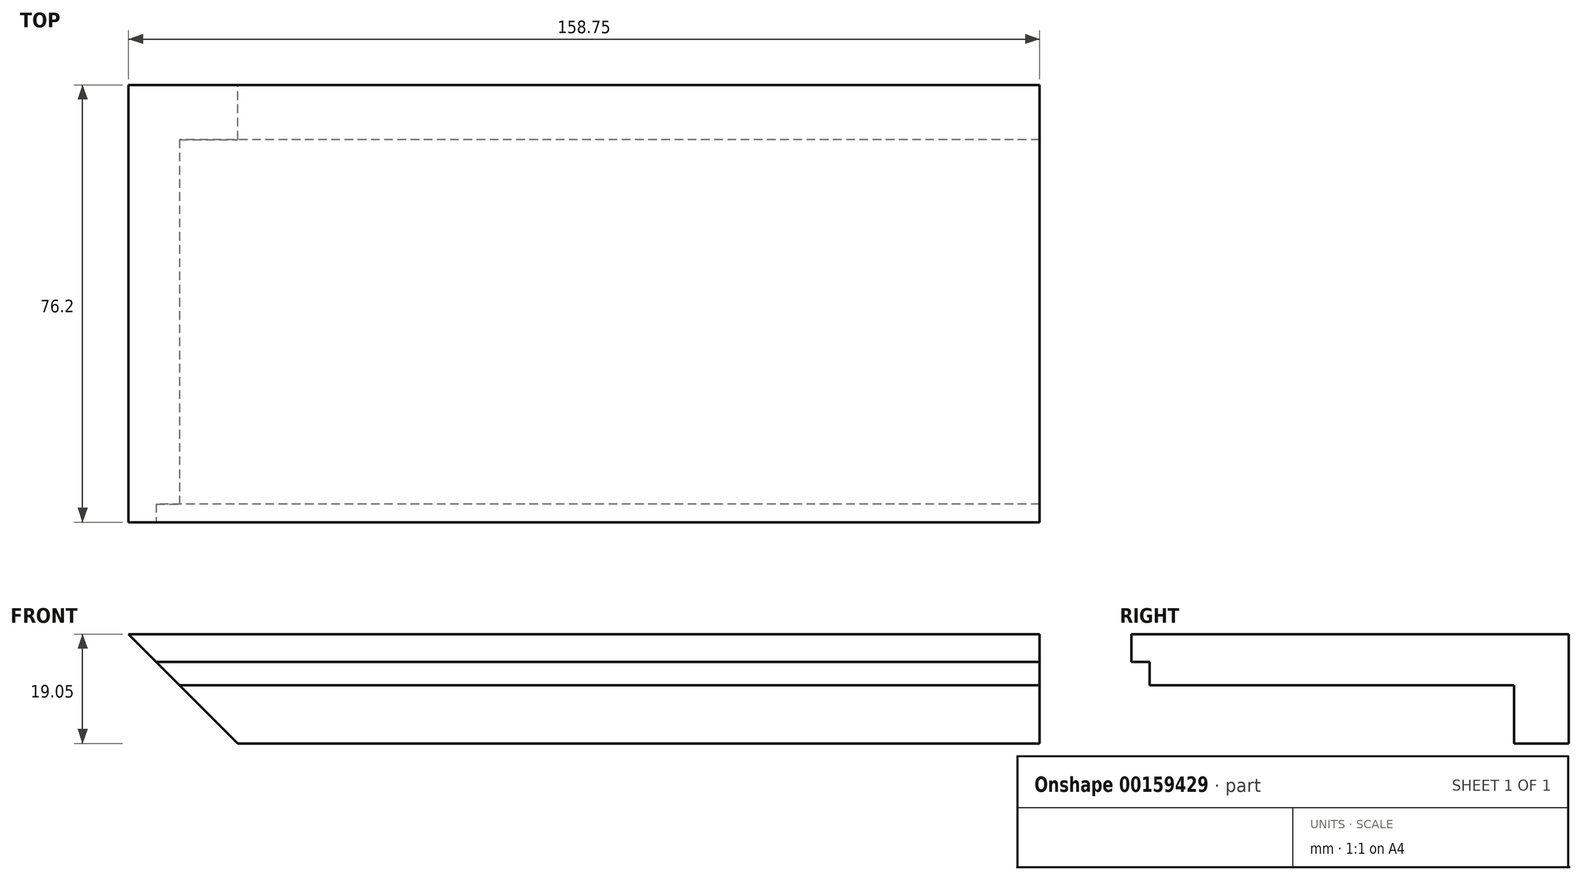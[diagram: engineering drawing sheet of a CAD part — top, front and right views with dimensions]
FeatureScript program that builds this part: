
annotation { "Feature Type Name" : "Feature", "Feature Type Description" : "" }
export const myFeature = defineFeature(function(context is Context, id is Id, definition is map)
    precondition{}
    {
        {
            var Q0;
            Q0=qCreatedBy(makeId("Front.planeOp"),FACE);
            var sketch = newSketch(context, id + "F0", { "sketchPlane" : qUnion([Q0])});
            skLineSegment(sketch, "E0", {"start": v(0, 180.55) * mm, "end": v(0, -185.02) * mm, "construction": true});
            skLineSegment(sketch, "E1", {"start": v(-187.82, 0) * mm, "end": v(184.46, 0) * mm, "construction": true});
            skLineSegment(sketch, "E2", {"start": v(0, 158.75) * mm, "end": v(-158.75, 158.75) * mm});
            skLineSegment(sketch, "E3", {"start": v(-158.75, 158.75) * mm, "end": v(-158.75, 0) * mm});
            skLineSegment(sketch, "E4", {"start": v(0, 139.7) * mm, "end": v(-139.7, 139.7) * mm});
            skLineSegment(sketch, "E5", {"start": v(-139.7, 139.7) * mm, "end": v(-139.7, 0) * mm});
            skLineSegment(sketch, "E6", {"start": v(-158.75, 0) * mm, "end": v(-139.7, 0) * mm});
            skLineSegment(sketch, "E7", {"start": v(0, 158.75) * mm, "end": v(0, 139.7) * mm});
            skSolve(sketch);
        }
        {
            var Q0;
            Q0=qSketchRegion(id+"F0",true);
            var Q1;
            Q1=qSketchRegion(id+"F2",true);
            extrude(context, id + "F1", {"entities" : qUnion([Q0, Q1]), "depth" : 76.2 * mm});
        }
        {
            var Q0;
            Q0=makeQuery(id+"F1.opExtrude","CAP_FACE",FACE,{"disambiguationData":[OSD([sQuery(id+"F0.wireOp",EDGE,"E2"),sQuery(id+"F0.wireOp",EDGE,"E3"),sQuery(id+"F0.wireOp",EDGE,"E4"),sQuery(id+"F0.wireOp",EDGE,"E5"),sQuery(id+"F0.wireOp",EDGE,"E6"),sQuery(id+"F0.wireOp",EDGE,"E7")])],"isStart":false});
            var sketch = newSketch(context, id + "F2", { "sketchPlane" : qUnion([Q0])});
            skLineSegment(sketch, "E8", {"start": v(0, -83.24) * mm, "end": v(0, 158.75) * mm, "construction": true});
            skLineSegment(sketch, "E9", {"start": v(-158.75, 0) * mm, "end": v(101.88, 0) * mm, "construction": true});
            skLineSegment(sketch, "E10.bottom", {"start": v(0, 0) * mm, "end": v(-153.92, 0) * mm});
            skLineSegment(sketch, "E10.top", {"start": v(0, 153.92) * mm, "end": v(-153.92, 153.92) * mm});
            skLineSegment(sketch, "E10.left", {"start": v(0, 0) * mm, "end": v(0, 153.92) * mm});
            skLineSegment(sketch, "E10.right", {"start": v(-153.92, 0) * mm, "end": v(-153.92, 153.92) * mm});
            skSolve(sketch);
        }
        {
            var Q0;
            Q0=qSketchRegion(id+"F2",true);
            extrude(context, id + "F3", {"entities" : qUnion([Q0]), "operationType" : NewBodyOperationType.REMOVE, "oppositeDirection" : true, "depth" : 3.17 * mm});
        }
        {
            var Q0;
            Q0=makeQuery(id+"F3.boolean.opBoolean","COPY",FACE,{"derivedFrom":makeQuery(id+"F3.opExtrude","CAP_FACE",FACE,{"disambiguationData":[OSD([sQuery(id+"F2.wireOp",EDGE,"E10.bottom"),sQuery(id+"F2.wireOp",EDGE,"E10.top"),sQuery(id+"F2.wireOp",EDGE,"E10.left"),sQuery(id+"F2.wireOp",EDGE,"E10.right")])],"isStart":false})});
            var sketch = newSketch(context, id + "F4", { "sketchPlane" : qUnion([Q0])});
            skLineSegment(sketch, "E11", {"start": v(0, 160.99) * mm, "end": v(0, -63.1) * mm, "construction": true});
            skLineSegment(sketch, "E12", {"start": v(-161.28, 0) * mm, "end": v(50.92, 0) * mm, "construction": true});
            skLineSegment(sketch, "E13.bottom", {"start": v(0, 0) * mm, "end": v(-149.86, 0) * mm});
            skLineSegment(sketch, "E13.top", {"start": v(0, 149.86) * mm, "end": v(-149.86, 149.86) * mm});
            skLineSegment(sketch, "E13.left", {"start": v(0, 0) * mm, "end": v(0, 149.86) * mm});
            skLineSegment(sketch, "E13.right", {"start": v(-149.86, 0) * mm, "end": v(-149.86, 149.86) * mm});
            skSolve(sketch);
        }
        {
            var Q0;
            Q0=qSketchRegion(id+"F4",true);
            extrude(context, id + "F5", {"entities" : qUnion([Q0]), "operationType" : NewBodyOperationType.REMOVE, "oppositeDirection" : true, "depth" : 63.5 * mm});
        }
        {
            var Q0;
            Q0=makeQuery(id+"F1.opExtrude","CAP_FACE",FACE,{"disambiguationData":[OSD([sQuery(id+"F0.wireOp",EDGE,"E2"),sQuery(id+"F0.wireOp",EDGE,"E3"),sQuery(id+"F0.wireOp",EDGE,"E4"),sQuery(id+"F0.wireOp",EDGE,"E5"),sQuery(id+"F0.wireOp",EDGE,"E6"),sQuery(id+"F0.wireOp",EDGE,"E7")])],"isStart":false});
            var sketch = newSketch(context, id + "F6", { "sketchPlane" : qUnion([Q0])});
            skPoint(sketch, "E14.0", {"position": v(-158.75, 158.75) * mm});
            skPoint(sketch, "E15.0", {"position": v(-139.7, 139.7) * mm});
            skPoint(sketch, "E16.0", {"position": v(-139.7, 0) * mm});
            skPoint(sketch, "E17.0", {"position": v(-158.75, 0) * mm});
            skLineSegment(sketch, "E18", {"start": v(-158.75, 158.75) * mm, "end": v(-139.7, 139.7) * mm});
            skLineSegment(sketch, "E19", {"start": v(-139.7, 139.7) * mm, "end": v(-139.7, 0) * mm});
            skLineSegment(sketch, "E20", {"start": v(-139.7, 0) * mm, "end": v(-158.75, 0) * mm});
            skLineSegment(sketch, "E21", {"start": v(-158.75, 0) * mm, "end": v(-158.75, 158.75) * mm});
            skSolve(sketch);
        }
        {
            var Q0;
            Q0 = qSketchRegion(id + "F6", true);
            extrude(context, id + "F7", {"entities" : qUnion([Q0]), "operationType" : NewBodyOperationType.REMOVE, "endBound" : BoundingType.THROUGH_ALL, "oppositeDirection" : true, "depth" : 25.4 * mm});
        }
    });
